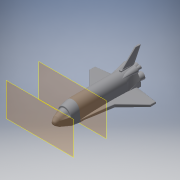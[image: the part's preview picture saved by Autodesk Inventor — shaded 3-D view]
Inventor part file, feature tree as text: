
AUTODESK INVENTOR PART (.ipt)
format: ipt  version: 2018 (Build 220112000, 112)  size: 2,012,160 bytes
history: native  units: in
note: dims shown in document units (in); Inventor stores cm internally (conversion verified against a paired STEP export)
features: sketch x28, plane x15, loft x11, extrude x8, fillet x6, other x3, projected_geometry x3, mirror x2, chamfer x2
ambient origin geometry x8: Origin, YZ Plane, XZ Plane, XY Plane, X Axis, Y Axis, Z Axis, Center Point
bodies: Solid1 (feature_tree)
feature tree (78):
  extrude  "Extrusion1"  TaperAngle=0.0deg  [1 undecoded]
  plane  "Work Plane1"
  plane  "Work Plane2"
  plane  "Work Plane3"
  loft  "Loft1"
  loft  "Loft2"
  fillet  "Fillet1"  Radius=240.6614in
  loft  "Loft4"
  fillet  "Fillet2"  Radius=125.0in
  extrude  "Extrusion2"  TaperAngle=0.0deg  [1 undecoded]
  extrude  "Extrusion3"  Depth=100.0in
  fillet  "Fillet3"  [1 undecoded]
  plane  "Work Plane4"
  mirror  "Mirror1"
  plane  "Work Plane5"
  sketch  "Sketch12"  dims[d36=0.0in d37=90.0deg d38=125.0in]
  loft  "Loft5"
  chamfer  "Chamfer1"  Angle=90.0deg  [1 undecoded]
  chamfer  "Chamfer2"  Angle=90.0deg  [1 undecoded]
  sketch  "Sketch15"  dims[d39=15.0in]
  plane  "Work Plane6"
  plane  "Work Plane7"
  loft  "Loft8"
  mirror  "Mirror2"
  extrude  "Extrusion5"  Depth=125.0in
  extrude  "Extrusion6"  TaperAngle=0.0deg  [1 undecoded]
  plane  "Work Plane8"
  sketch  "Sketch20"  dims[d51=10.0in]
  plane  "Work Plane10"
  loft  "Loft9"
  fillet  "Fillet4"  Radius=84.0in
  extrude  "Extrusion7"  Depth=0.6803in
  fillet  "Fillet5"  Radius=48.0in
  fillet  "Fillet6"  Radius=6500.0in
  sketch  "Sketch23"  dims[d55=0.0in]
  plane  "Work Plane11"
  sketch  "Sketch24"  dims[d56=0.0in]
  loft  "Loft10"
  loft  "Loft11"
  sketch  "Sketch27"  dims[d64=60.0in d70=125.0in]
  plane  "Work Plane12"
  loft  "Loft12"
  loft  "Loft13"
  loft  "Loft14"
  sketch  "Sketch31"  dims[d89=6500.0in d90=7700.0in]
  plane  "Work Plane13"
  sketch  "Sketch32"  dims[d91=10.0in d92=345.0in d93=0.0in]
  sketch  "Sketch33"  dims[d94=10.0in d95=125.0in]
  plane  "Work Plane14"
  extrude  "Extrusion8"  Depth=245.0in
  sketch  "Sketch35"  dims[d98=10.0in d99=0.0in]
  plane  "Work Plane15"
  extrude  "Extrusion9"  Depth=90.0in
  plane  "Work Plane16"
  sketch  "Sketch1"  dims[d5=250.0in d12=0.0in]
  sketch  "Sketch2"  dims[d13=75.0in d15=110.0in]
  other  "Edges1"
  sketch  "Sketch3"  dims[d21=98.0in d24=110.0in d25=240.6614in]
  sketch  "Sketch6"  dims[d26=730.0in d27=0.0in d28=300.0in d29=125.0in]
  sketch  "Sketch7"  dims[d30=250.0in d31=0.0in]
  other  "Edges3"
  sketch  "Sketch8"  dims[d32=125.0in d33=100.0in d34=0.0in d35=90.0deg]
  other  "Edges4"
  sketch  "Sketch17"  dims[d40=20.0in]
  sketch  "Sketch18"  dims[d41=10.0in]
  sketch  "Sketch19"  dims[d50=15.0in]
  projected_geometry  "Projected Loop7"
  sketch  "Sketch21"  dims[d52=75.0in]
  sketch  "Sketch22"  dims[d54=125.0in]
  sketch  "Sketch25"  dims[d57=0.0in d58=0.0in d59=90.0deg d60=0.0in d61=90.0deg]
  sketch  "Sketch26"  dims[d62=10.65in d63=50.0in]
  sketch  "Sketch28"  dims[d71=50.0in d72=0.0in d73=90.0deg]
  sketch  "Sketch29"  dims[d74=0.0in d75=90.0deg d76=40.0in d79=84.0in]
  sketch  "Sketch30"  dims[d80=0.0in d82=0.6803in d83=48.0in d84=0.0in d85=6500.0in]
  sketch  "Sketch34"  dims[d96=200.0in d97=0.0in]
  projected_geometry  "Projected Loop8"
  projected_geometry  "Projected Loop9"
  sketch  "Sketch36"  dims[d100=0.0in d101=245.0in d102=90.0in d105=15.0in d106=0.0618in d107=45.0deg d108=345.0in d109=0.0in d110=90.0deg d111=0.0in d112=90.0deg d113=5.2in d114=0.125in d115=45.0deg d116=5.2in d117=0.125in d118=45.0deg d119=-200.0in d126=100.0in d127=25.0in d133=-205.0in d134=50.0in d135=60.0in d137=0.0in d138=90.0deg d139=0.0in d140=90.0deg d141=160.0in d142=100.0in d143=0.6528in d144=0.0in d145=0.0in d146=9000.0in d147=0.0in d148=15.0in d149=25.0in d150=0.0in d151=30.0in d152=0.0in d153=-20.0in d154=30.0in d155=10.0in d156=1.2162in d157=1.2162in d158=195.0in d160=225.0in d166=30.0in d167=225.0in d168=20.0in d169=30.0in d170=20.0in d171=80.0in d172=0.0in d173=90.0deg d174=0.0in d175=90.0deg d176=7.0in d177=0.1374in d178=200.0in d179=0.0in d180=9.475in d184=150.0in d185=150.0in d186=9.475in d187=40.0in d188=80.0in d189=65.0in d190=60.0in d191=20.0in d192=125.0in d193=0.0in d194=13.0in d195=32.0in d196=55.0in d197=55.0in d198=55.0in d199=80.0in d200=95.0in d201=95.0in d202=40.0in d203=0.0in d204=90.0deg d205=0.0in d206=90.0deg d207=0.0in d208=90.0deg d209=0.0in d210=90.0deg d211=25.0in d212=90.0in d213=8.0in d214=0.0in d215=90.0deg d216=0.0in d217=90.0deg d218=105.0in d219=5.0in d220=5.0in d221=0.0in d222=90.0deg d223=0.0in d224=90.0deg d225=105.0in d226=5.0in d227=5.0in d228=0.0in d229=90.0deg d230=0.0in d231=90.0deg d232=-20.0in d233=90.0deg d234=95.0in d235=0.0in d236=90.0deg d237=105.0in d238=0.0in d239=500.0in]
note: 6 required parameter values undecoded (feature->parameter linkage not recoverable at this tier; creation-order binding heuristic only, values carry confidence <= 0.55)
